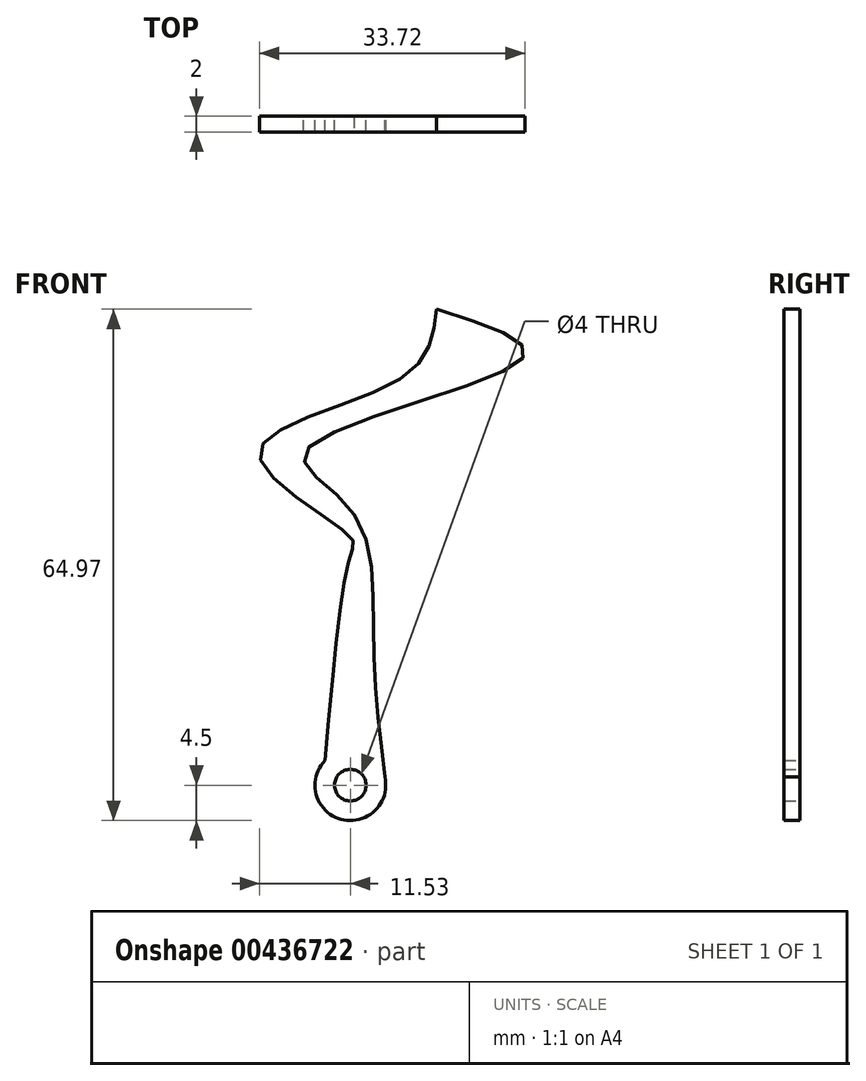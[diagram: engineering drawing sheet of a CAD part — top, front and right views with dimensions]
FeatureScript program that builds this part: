
annotation { "Feature Type Name" : "Feature", "Feature Type Description" : "" }
export const myFeature = defineFeature(function(context is Context, id is Id, definition is map)
    precondition{}
    {
        {
            var Q0;
            Q0=qCreatedBy(makeId("Front.planeOp"),FACE);
            var sketch = newSketch(context, id + "F0", { "sketchPlane" : qUnion([Q0])});
            skCircle(sketch, "E0", {"center": v(0, 0) * mm, "radius": 2 * mm});
            skArc(sketch, "E1", {"start": v(-3.23, 3.13) * mm, "mid": v(-1.19, -4.34) * mm, "end": v(4.38, 1.05) * mm});
            skFitSpline(sketch, "E2", {"points": [v(-3.23, 3.13) * mm, v(0, 29.21) * mm, v(0, 31.55) * mm, v(-11.53, 42.1) * mm, v(6.45, 51.68) * mm, v(10.94, 60.47) * mm], "startDerivative": vector(10.72, 119.84) * mm, "endDerivative": vector(6.16, 55.21) * mm});
            skFitSpline(sketch, "E3", {"points": [v(4.5, 0) * mm, v(2.93, 18.85) * mm, v(0, 35.07) * mm, v(-5.67, 42.5) * mm, v(21.88, 54.22) * mm, v(10.94, 60.47) * mm], "startDerivative": vector(-10.41, 88.14) * mm, "endDerivative": vector(-110.26, 34.29) * mm});
            skSolve(sketch);
        }
        {
            var Q0;
            Q0 = qSketchRegion(id + "F0", true);
            extrude(context, id + "F1", {"entities" : qUnion([Q0]), "depth" : 2 * mm});
        }
    });
